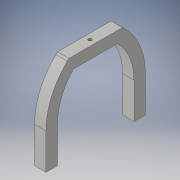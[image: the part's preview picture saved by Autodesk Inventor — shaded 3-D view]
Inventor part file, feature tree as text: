
AUTODESK INVENTOR PART (.ipt)
format: ipt  version: 2016 (Build 200138000, 138)  size: 134,656 bytes
history: native  units: in
note: dims shown in document units (in); Inventor stores cm internally (conversion verified against a paired STEP export)
features: sketch x4, sweep x1, extrude x1, hole x1
ambient origin geometry x8: Origin, YZ Plane, XZ Plane, XY Plane, X Axis, Y Axis, Z Axis, Center Point
bodies: Solid1 (feature_tree)
feature tree (7):
  sweep  "Sweep1"
  extrude  "Extrusion1"  Depth=0.35in
  hole  "Hole1"  [1 undecoded]
  sketch  "Sketch1"  dims[d0=2.7in d1=0.35in]
  sketch  "Sketch2"  dims[d2=0.35in d3=0.35in]
  sketch  "Sketch3"  dims[d4=2.5in d8=0.0in d9=0.0in]
  sketch  "Sketch5"  dims[d10=0.1in d11=0.1in d12=0.175in d13=1.35in d14=0.175in d15=1.35in d16=0.35in d17=0.0in d21=1.5in d22=1.1in d23=1.1in d24=0.1in d25=0.1in d26=0.75in d27=0.375in d28=0.25in d29=0.5635in d30=1.0in d31=0.8108in]
note: 1 required parameter value undecoded (feature->parameter linkage not recoverable at this tier; creation-order binding heuristic only, values carry confidence <= 0.55)
